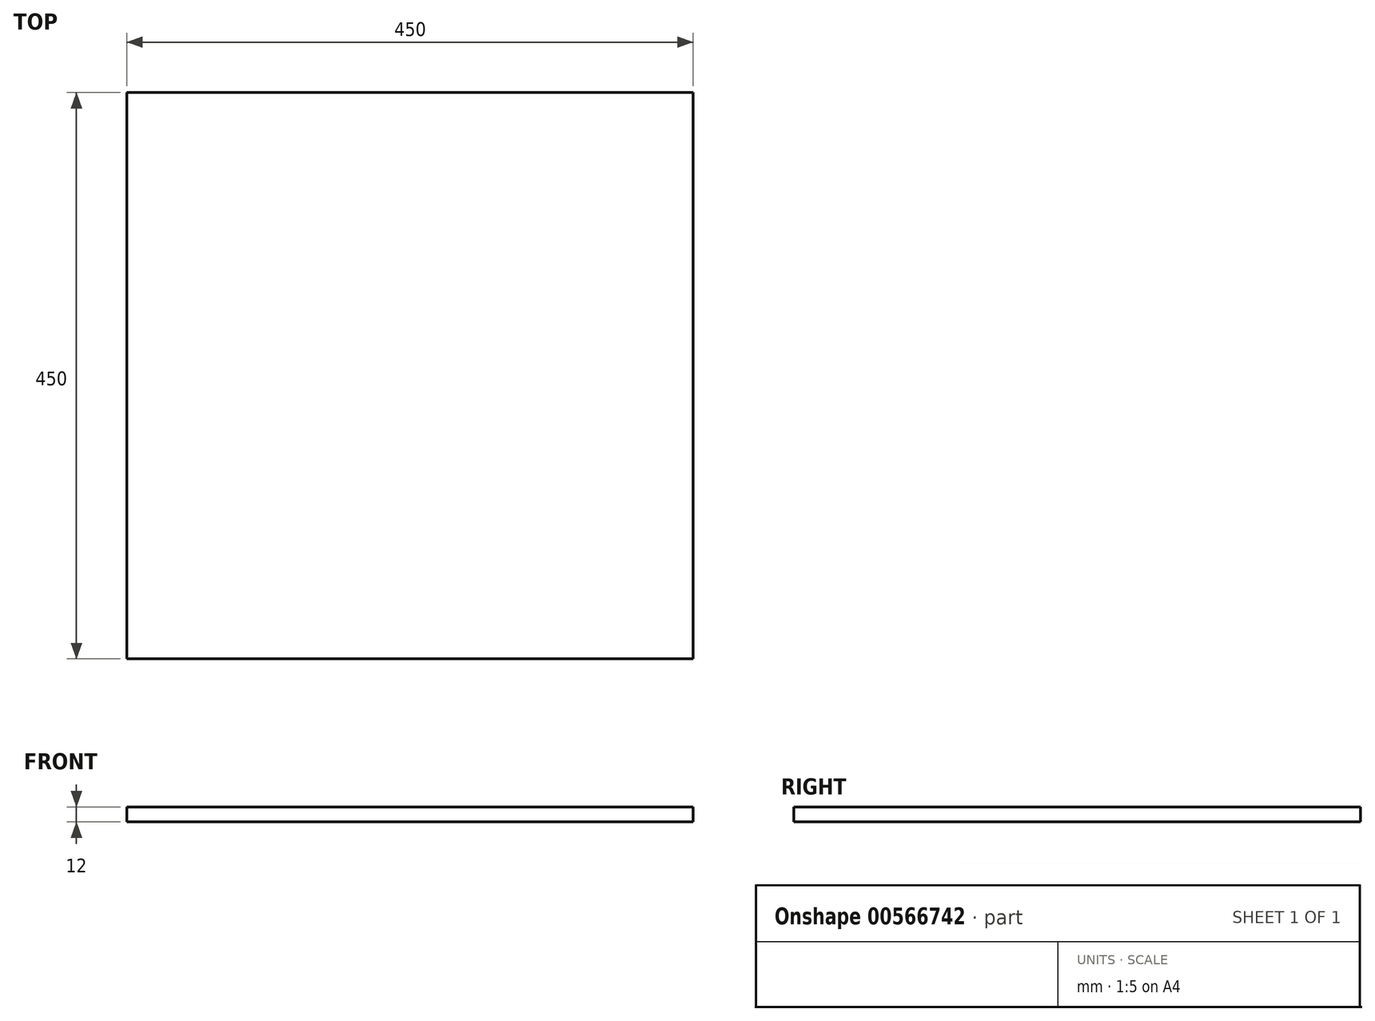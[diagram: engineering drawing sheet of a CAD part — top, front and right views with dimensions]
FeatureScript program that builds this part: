
annotation { "Feature Type Name" : "Feature", "Feature Type Description" : "" }
export const myFeature = defineFeature(function(context is Context, id is Id, definition is map)
    precondition{}
    {
        {
            var Q0;
            Q0=qCreatedBy(makeId("Top.planeOp"),FACE);
            var sketch = newSketch(context, id + "F0", { "sketchPlane" : qUnion([Q0])});
            skLineSegment(sketch, "E0.bottom", {"start": v(225, -225) * mm, "end": v(-225, -225) * mm});
            skLineSegment(sketch, "E0.top", {"start": v(225, 225) * mm, "end": v(-225, 225) * mm});
            skLineSegment(sketch, "E0.left", {"start": v(225, -225) * mm, "end": v(225, 225) * mm});
            skLineSegment(sketch, "E0.right", {"start": v(-225, -225) * mm, "end": v(-225, 225) * mm});
            skPoint(sketch, "E0.middle", {"position": v(0, 0) * mm});
            skSolve(sketch);
        }
        {
            var Q0;
            Q0 = qSketchRegion(id + "F0", true);
            extrude(context, id + "F1", {"entities" : qUnion([Q0]), "depth" : 12 * mm, "offsetDistance" : 25 * mm});
        }
    });
